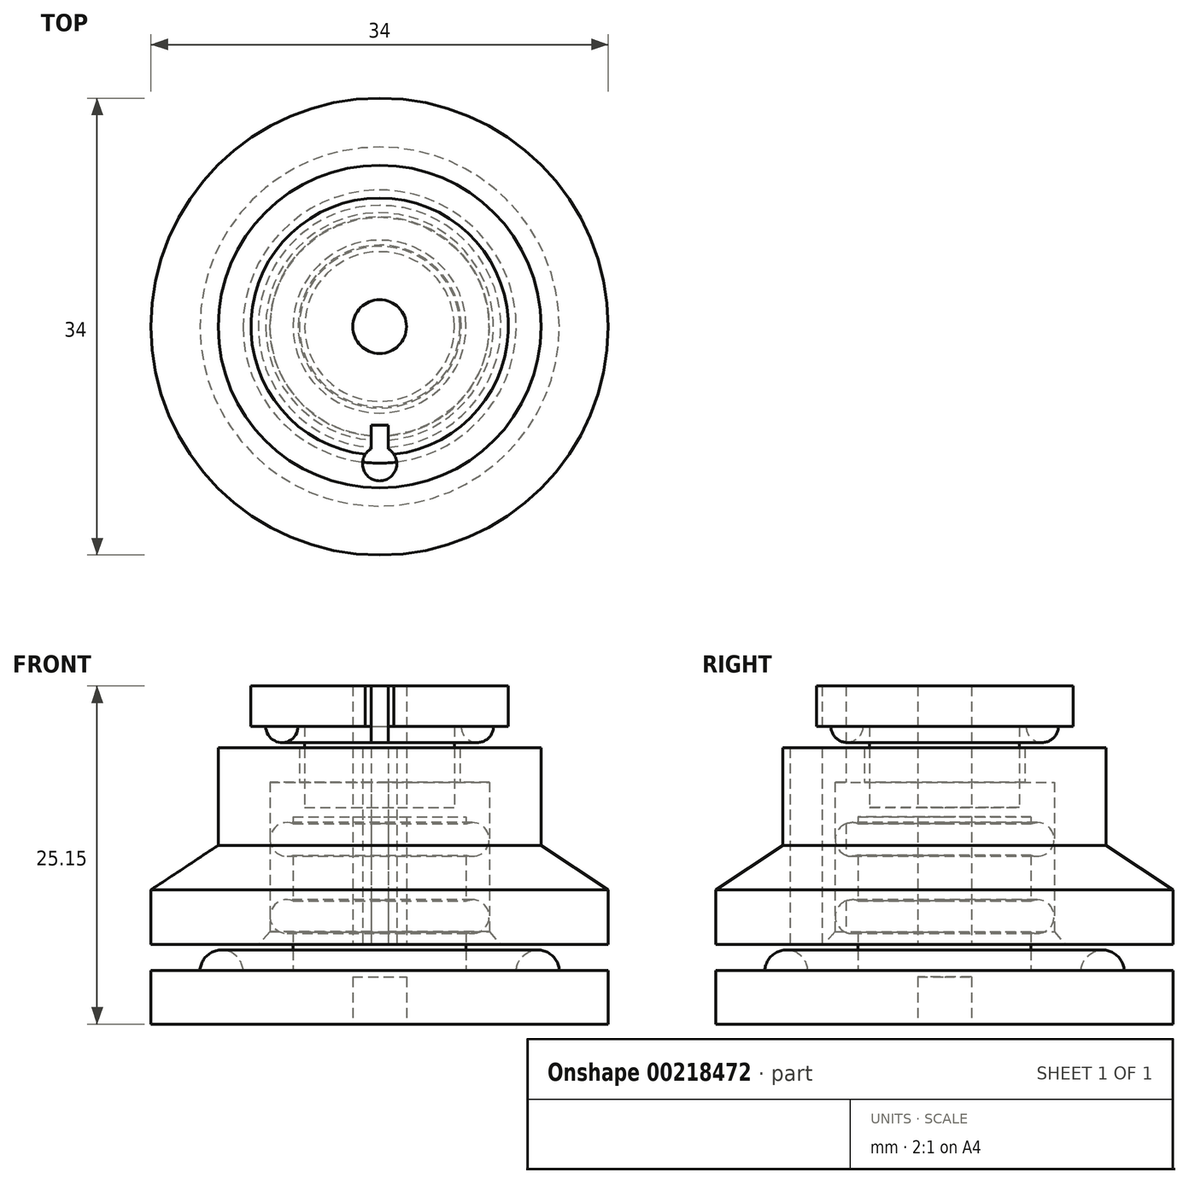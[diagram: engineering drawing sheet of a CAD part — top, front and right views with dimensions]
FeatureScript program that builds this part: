
annotation { "Feature Type Name" : "Feature", "Feature Type Description" : "" }
export const myFeature = defineFeature(function(context is Context, id is Id, definition is map)
    precondition{}
    {
        {
            var Q0;
            Q0=qCreatedBy(makeId("Front.planeOp"),FACE);
            var sketch = newSketch(context, id + "F0", { "sketchPlane" : qUnion([Q0])});
            skLineSegment(sketch, "E0", {"start": v(-17, 0) * mm, "end": v(-2, 0) * mm});
            skLineSegment(sketch, "E1", {"start": v(0, 3.5) * mm, "end": v(0, 5.92) * mm});
            skLineSegment(sketch, "E2", {"start": v(-6.43, 4) * mm, "end": v(-9.88, 4) * mm});
            skLineSegment(sketch, "E3", {"start": v(-17, 4) * mm, "end": v(-17, 0) * mm});
            skLineSegment(sketch, "E4.0", {"start": v(-9.02, 5.91) * mm, "end": v(-17, 5.91) * mm});
            skLineSegment(sketch, "E4.1", {"start": v(-8.16, 18) * mm, "end": v(-8.16, 6.88) * mm});
            skLineSegment(sketch, "E4.2", {"start": v(-5.97, 18) * mm, "end": v(-8.16, 18) * mm});
            skLineSegment(sketch, "E5.1", {"start": v(-12, 20.55) * mm, "end": v(-12, 13.3) * mm});
            skLineSegment(sketch, "E5.2", {"start": v(-5.97, 20.55) * mm, "end": v(-12, 20.55) * mm});
            skLineSegment(sketch, "E6", {"start": v(-17, 5.91) * mm, "end": v(-17, 10) * mm});
            skLineSegment(sketch, "E7.trimOffspring", {"start": v(-6.43, 12.57) * mm, "end": v(-6.43, 9.17) * mm});
            skLineSegment(sketch, "E8.trimOffspring", {"start": v(-6.43, 5.6) * mm, "end": v(-6.43, 4) * mm});
            skLineSegment(sketch, "E9.trimOffspring", {"start": v(-13.88, 4) * mm, "end": v(-17, 4) * mm});
            skArc(sketch, "E10.0", {"start": v(-10.16, 4) * mm, "mid": v(-11.76, 5.51) * mm, "end": v(-13.36, 4) * mm});
            skLineSegment(sketch, "E11", {"start": v(-13.88, 4) * mm, "end": v(-13.36, 4) * mm});
            skLineSegment(sketch, "E12", {"start": v(-10.16, 4) * mm, "end": v(-9.88, 4) * mm});
            skArc(sketch, "E13.0", {"start": v(-6.43, 14.9) * mm, "mid": v(-8.15, 13.74) * mm, "end": v(-6.43, 12.57) * mm});
            skLineSegment(sketch, "E14", {"start": v(-6.43, 14.9) * mm, "end": v(-6.43, 15.42) * mm});
            skArc(sketch, "E15.0", {"start": v(-6.43, 9.17) * mm, "mid": v(-8.15, 8) * mm, "end": v(-6.43, 6.83) * mm});
            skLineSegment(sketch, "E16", {"start": v(-6.43, 6.83) * mm, "end": v(-6.43, 5.6) * mm});
            skLineSegment(sketch, "E17", {"start": v(-2, 15.42) * mm, "end": v(-2, 5.92) * mm});
            skLineSegment(sketch, "E18", {"start": v(-2, 5.92) * mm, "end": v(0, 5.92) * mm});
            skLineSegment(sketch, "E19.0", {"start": v(-5.97, 20.55) * mm, "end": v(-5.97, 18) * mm});
            skLineSegment(sketch, "E20.trimOffspring", {"start": v(-2, 15.42) * mm, "end": v(-6.43, 15.42) * mm});
            skLineSegment(sketch, "E21", {"start": v(-5.57, 16.12) * mm, "end": v(-2, 16.12) * mm});
            skLineSegment(sketch, "E22", {"start": v(-2, 16.12) * mm, "end": v(-2, 25.15) * mm});
            skLineSegment(sketch, "E23", {"start": v(-5.57, 22.15) * mm, "end": v(-6.07, 22.15) * mm});
            skLineSegment(sketch, "E24", {"start": v(-9.57, 22.15) * mm, "end": v(-9.57, 25.15) * mm});
            skLineSegment(sketch, "E25", {"start": v(-2, 25.15) * mm, "end": v(-9.57, 25.15) * mm});
            skLineSegment(sketch, "E26", {"start": v(-5.57, 22.15) * mm, "end": v(-5.57, 16.12) * mm});
            skArc(sketch, "E27", {"start": v(-8.47, 22.15) * mm, "mid": v(-7.27, 20.95) * mm, "end": v(-6.07, 22.15) * mm});
            skLineSegment(sketch, "E28.trimOffspring", {"start": v(-8.47, 22.15) * mm, "end": v(-9.57, 22.15) * mm});
            skLineSegment(sketch, "E29", {"start": v(-17, 10) * mm, "end": v(-12, 13.3) * mm});
            skLineSegment(sketch, "E30", {"start": v(-8.16, 6.88) * mm, "end": v(-9.02, 5.91) * mm});
            skLineSegment(sketch, "E31", {"start": v(-2, 0) * mm, "end": v(-2, 3.5) * mm});
            skLineSegment(sketch, "E32", {"start": v(-2, 3.5) * mm, "end": v(0, 3.5) * mm});
            skPoint(sketch, "E33.orphan", {"position": v(0, 0) * mm});
            skSolve(sketch);
        }
        {
            var Q0;
            Q0=makeQuery(id+"F0.imprint","IMPRINT",FACE,{"disambiguationData":[TD([[makeQuery(id+"F0.imprint","IMPRINT",EDGE,{"derivedFrom":sQuery(id+"F0.wireOp",EDGE,"E0")}),1.0]])]});
            var Q1;
            Q1=sQuery(id+"F0.wireOp",EDGE,"E1");
            revolve(context, id + "F1", {"entities" : qUnion([Q0]), "axis" : qUnion([Q1]), "revolveType" : RevolveType.FULL});
        }
        {
            var Q0;
            Q0=makeQuery(id+"F0.imprint","IMPRINT",FACE,{"disambiguationData":[TD([[makeQuery(id+"F0.imprint","IMPRINT",EDGE,{"derivedFrom":sQuery(id+"F0.wireOp",EDGE,"E4.0")}),-1.0]])]});
            var Q1;
            Q1=sQuery(id+"F0.wireOp",EDGE,"E1");
            revolve(context, id + "F2", {"entities" : qUnion([Q0]), "axis" : qUnion([Q1]), "revolveType" : RevolveType.FULL});
        }
        {
            var Q0;
            Q0=makeQuery(id+"F0.imprint","IMPRINT",FACE,{"disambiguationData":[TD([[makeQuery(id+"F0.imprint","IMPRINT",EDGE,{"derivedFrom":sQuery(id+"F0.wireOp",EDGE,"E21")}),1.0]])]});
            var Q1;
            Q1=sQuery(id+"F0.wireOp",EDGE,"E1");
            revolve(context, id + "F3", {"entities" : qUnion([Q0]), "axis" : qUnion([Q1]), "revolveType" : RevolveType.FULL});
        }
        {
            var Q0;
            Q0=makeQuery(id+"F2.opRevolve","SWEPT_FACE",FACE,{"disambiguationData":[OSD([sQuery(id+"F0.wireOp",EDGE,"E4.0")])]});
            cPlane(context, id + "F4", {"entities" : qUnion([Q0]), "cplaneType" : CPlaneType.OFFSET, "offset" : 0 * mm, "width" : 150 * mm, "height" : 150 * mm});
        }
        {
            var Q0;
            Q0=qCreatedBy(id+"F4.planeOp",FACE);
            var sketch = newSketch(context, id + "F5", { "sketchPlane" : qUnion([Q0])});
            skLineSegment(sketch, "E34", {"start": v(0, 0) * mm, "end": v(0, 9.25) * mm, "construction": true});
            skLineSegment(sketch, "E35.bottom", {"start": v(0.64, 7.32) * mm, "end": v(-0.64, 7.32) * mm});
            skLineSegment(sketch, "E35.left", {"start": v(0.64, 7.32) * mm, "end": v(0.64, 9.1) * mm});
            skLineSegment(sketch, "E35.right", {"start": v(-0.64, 7.32) * mm, "end": v(-0.64, 9.1) * mm});
            skPoint(sketch, "E35.middle", {"position": v(0, 9.25) * mm});
            skArc(sketch, "E36", {"start": v(0.64, 9.1) * mm, "mid": v(0, 11.48) * mm, "end": v(-0.64, 9.1) * mm});
            skLineSegment(sketch, "E37.trimOffspring", {"start": v(0, 11.18) * mm, "end": v(0, 18.5) * mm, "construction": true});
            skSolve(sketch);
        }
        {
            var Q0;
            Q0=makeQuery(id+"F5.imprint","IMPRINT",FACE,{"disambiguationData":[TD([[makeQuery(id+"F5.imprint","IMPRINT",EDGE,{"derivedFrom":sQuery(id+"F5.wireOp",EDGE,"E35.bottom")}),-1.0]])]});
            extrude(context, id + "F6", {"entities" : qUnion([Q0]), "operationType" : NewBodyOperationType.REMOVE, "endBound" : BoundingType.THROUGH_ALL, "oppositeDirection" : true, "depth" : 10 * mm});
        }
    });
